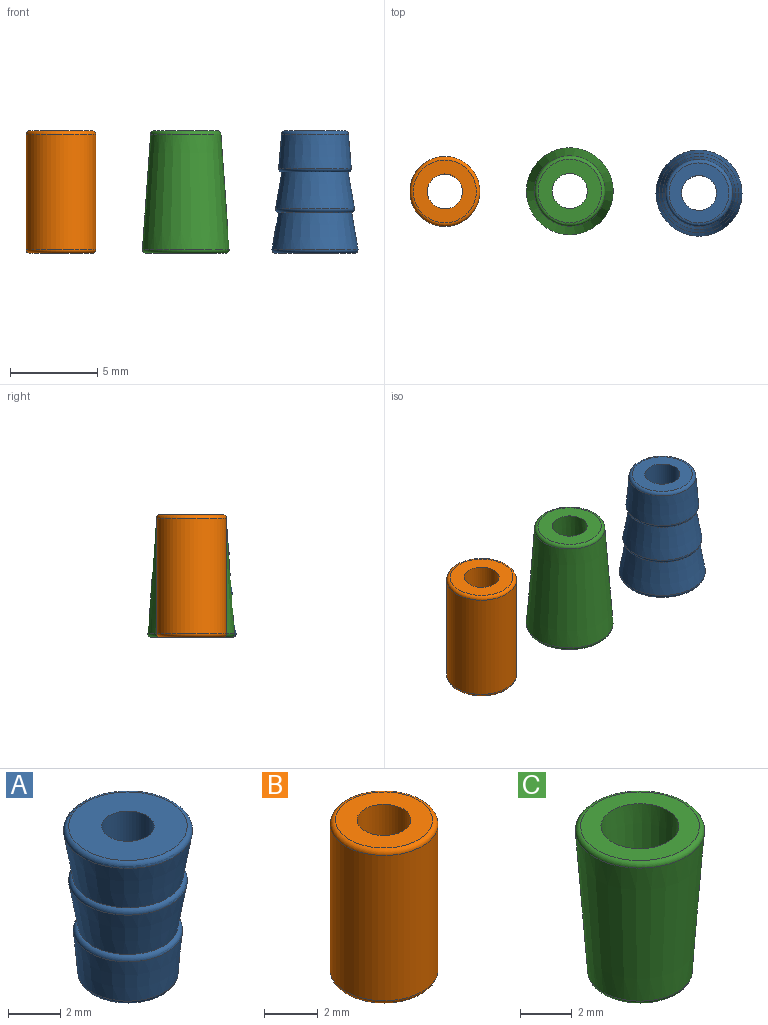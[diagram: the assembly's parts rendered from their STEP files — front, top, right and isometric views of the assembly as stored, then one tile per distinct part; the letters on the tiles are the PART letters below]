
ASSEMBLY  parts=3 mates=2
PART A: 10 faces, bbox 5.3x5.3x7 mm
  f0: cylinder r=1mm len=7mm, axis (0,0,1), area 44mm2, adj f1,f5
  f1: plane 3.43x3.43mm, normal (0,0,-1), area 6.1mm2, adj f0,f6
  f2: cone r=1.9mm half-angle=4.9deg, axis (0,0,1), area 24.6mm2, adj f6,f7
  f3: cone r=1.9mm half-angle=9.8deg, axis (0,0,1), area 27.8mm2, adj f7,f8
  f4: cone r=2.1mm half-angle=9.8deg, axis (0,0,1), area 30.4mm2, adj f8,f9
  f5: plane 4.53x4.53mm, normal (0,0,1), area 12.9mm2, adj f0,f9
  f6: torus R=1.72mm, axis (0,0,1), area 3.4mm2, adj f1,f2
  f7: torus R=1.88mm, axis (0,0,1), area 4mm2, adj f2,f3
  f8: torus R=2.06mm, axis (0,0,1), area 4.3mm2, adj f3,f4
  f9: torus R=2.26mm, axis (0,0,-1), area 5.2mm2, adj f4,f5
PART B: 6 faces, bbox 4.3x4.3x7 mm
  f0: cylinder r=1mm len=7mm, axis (0,0,-1), area 44mm2, adj f2,f3
  f1: cylinder r=2mm len=6.6mm, axis (0,0,-1), area 82.9mm2, adj f4,f5
  f2: plane 3.6x3.6mm, normal (0,0,1), area 7mm2, adj f0,f5
  f3: plane 3.6x3.6mm, normal (0,0,-1), area 7mm2, adj f0,f4
  f4: torus R=1.8mm, axis (0,0,1), area 3.8mm2, adj f1,f3
  f5: torus R=1.8mm, axis (0,0,1), area 3.8mm2, adj f1,f2
PART C: 6 faces, bbox 5.4x5.4x7 mm
  f0: cone r=1.5mm half-angle=4.1deg, axis (0,0,1), area 55.1mm2, adj f1,f3
  f1: plane 3.63x3.63mm, normal (0,0,-1), area 7.2mm2, adj f0,f4
  f2: cone r=2mm half-angle=4.1deg, axis (0,0,1), area 93.5mm2, adj f4,f5
  f3: plane 4.57x4.57mm, normal (0,0,1), area 9.3mm2, adj f0,f5
  f4: torus R=1.81mm, axis (0,0,1), area 3.7mm2, adj f1,f2
  f5: torus R=2.29mm, axis (0,0,-1), area 5mm2, adj f2,f3
PLACE A rot(axis=(1,0,0),180deg) t=(14.55,-0.09,7)mm
PLACE B at identity
PLACE C rot(axis=(1,0,0),180deg) t=(7.15,0.02,7)mm
MATE planar C.f2 <-> B.f1  axis (0,0,-1) through (7.15,0.02,0)mm
MATE planar A.f9 <-> B.f1  axis (0,0,-1) through (14.55,-0.09,0)mm
